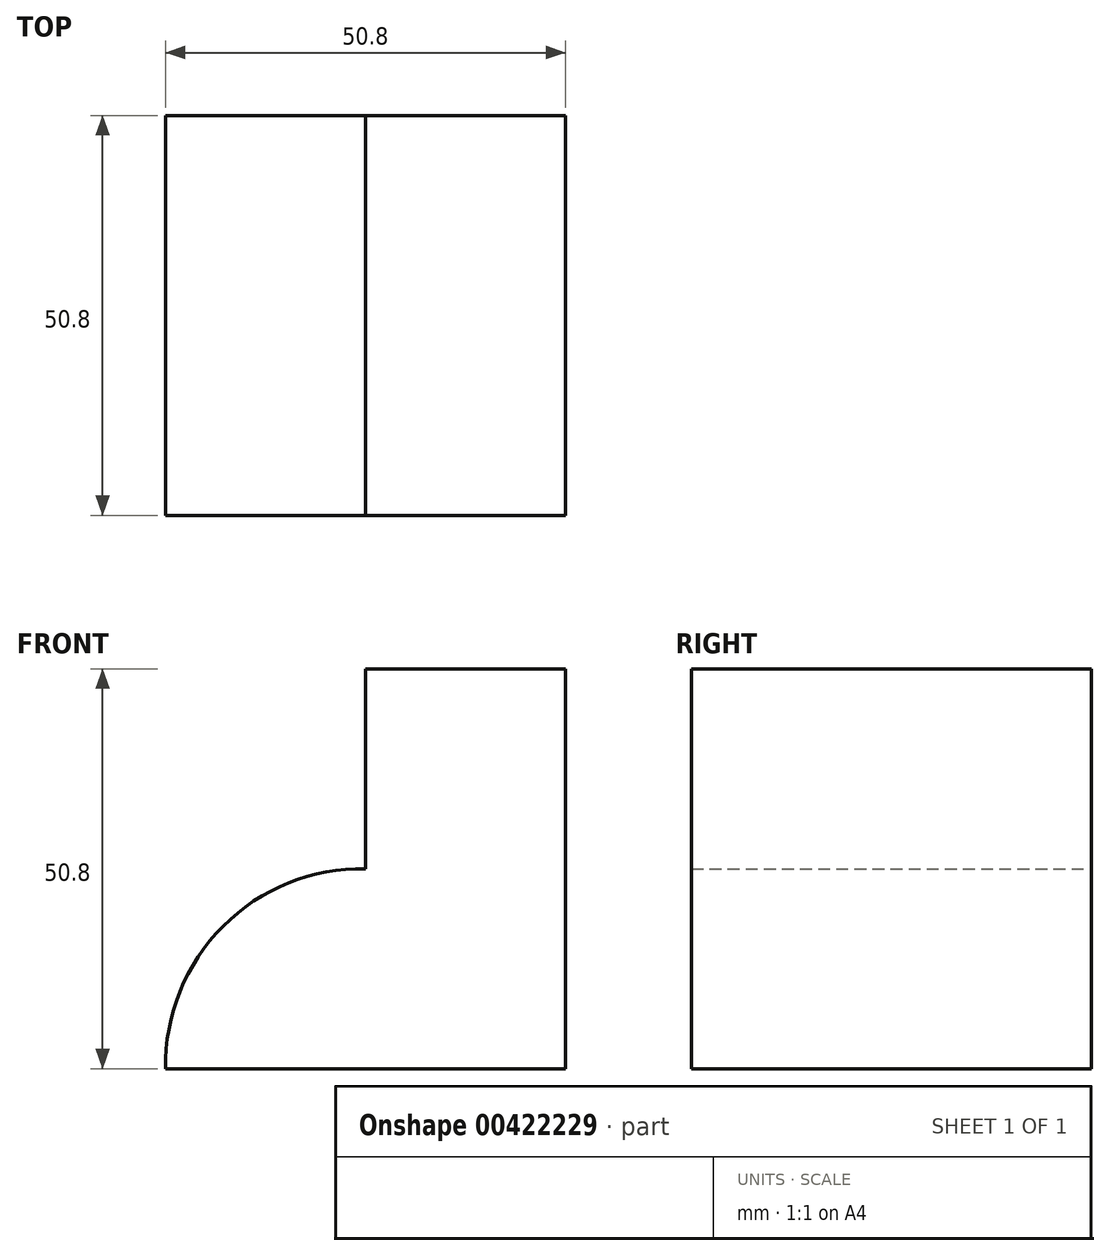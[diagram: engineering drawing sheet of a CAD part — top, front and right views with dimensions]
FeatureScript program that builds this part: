
annotation { "Feature Type Name" : "Feature", "Feature Type Description" : "" }
export const myFeature = defineFeature(function(context is Context, id is Id, definition is map)
    precondition{}
    {
        {
            var Q0;
            Q0=qCreatedBy(makeId("Front.planeOp"),FACE);
            var sketch = newSketch(context, id + "F0", { "sketchPlane" : qUnion([Q0])});
            skLineSegment(sketch, "E0", {"start": v(-12.73, 25.68) * mm, "end": v(-12.73, 51.08) * mm});
            skLineSegment(sketch, "E1", {"start": v(-12.73, 51.08) * mm, "end": v(12.67, 51.08) * mm});
            skLineSegment(sketch, "E2", {"start": v(12.67, 51.08) * mm, "end": v(12.67, 0.28) * mm});
            skLineSegment(sketch, "E3", {"start": v(12.67, 0.28) * mm, "end": v(-38.13, 0.28) * mm});
            skArc(sketch, "E4", {"start": v(-12.73, 25.68) * mm, "mid": v(-30.83, 18.38) * mm, "end": v(-38.13, 0.28) * mm});
            skSolve(sketch);
        }
        {
            var Q0;
            Q0 = qSketchRegion(id + "F0", true);
            extrude(context, id + "F1", {"entities" : qUnion([Q0]), "depth" : 50.8 * mm});
        }
    });
